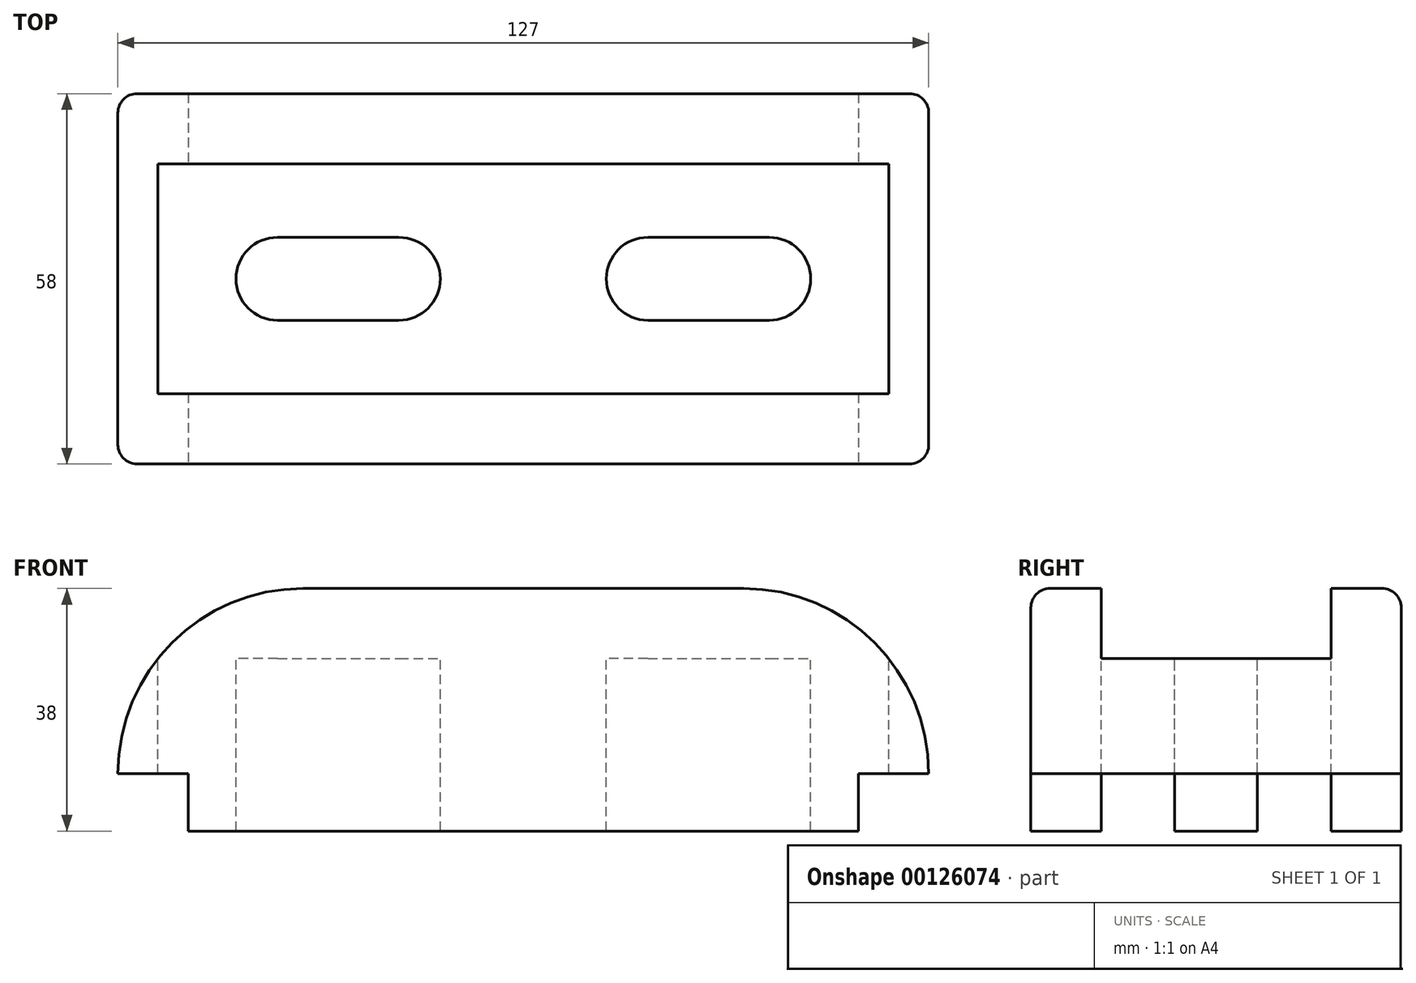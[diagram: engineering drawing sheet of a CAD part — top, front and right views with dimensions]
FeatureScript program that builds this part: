
annotation { "Feature Type Name" : "Feature", "Feature Type Description" : "" }
export const myFeature = defineFeature(function(context is Context, id is Id, definition is map)
    precondition{}
    {
        {
            var Q0;
            Q0=qCreatedBy(makeId("Front.planeOp"),FACE);
            var sketch = newSketch(context, id + "F0", { "sketchPlane" : qUnion([Q0])});
            skLineSegment(sketch, "E0", {"start": v(11, 0) * mm, "end": v(11, 9) * mm});
            skLineSegment(sketch, "E1", {"start": v(11, 9) * mm, "end": v(0, 9) * mm});
            skLineSegment(sketch, "E2", {"start": v(11, 0) * mm, "end": v(116, 0) * mm});
            skLineSegment(sketch, "E3", {"start": v(116, 0) * mm, "end": v(116, 9) * mm});
            skLineSegment(sketch, "E4", {"start": v(116, 9) * mm, "end": v(127, 9) * mm});
            skArc(sketch, "E5", {"start": v(29, 38) * mm, "mid": v(8.5, 29.5) * mm, "end": v(0, 9) * mm});
            skArc(sketch, "E6", {"start": v(127, 9) * mm, "mid": v(118.5, 29.5) * mm, "end": v(98, 38) * mm});
            skLineSegment(sketch, "E7", {"start": v(29, 38) * mm, "end": v(98, 38) * mm});
            skSolve(sketch);
        }
        {
            var Q0;
            Q0=makeQuery(id+"F0.imprint","IMPRINT",FACE,{"disambiguationData":[TD([[makeQuery(id+"F0.imprint","IMPRINT",EDGE,{"derivedFrom":sQuery(id+"F0.wireOp",EDGE,"E0")}),-1.0]])]});
            extrude(context, id + "F1", {"entities" : qUnion([Q0]), "oppositeDirection" : true, "depth" : 58 * mm});
        }
        {
            var Q0;
            Q0=qCreatedBy(makeId("Right.planeOp"),FACE);
            var sketch = newSketch(context, id + "F2", { "sketchPlane" : qUnion([Q0])});
            skLineSegment(sketch, "E8.bottom", {"start": v(11, 38) * mm, "end": v(47, 38) * mm});
            skLineSegment(sketch, "E8.top", {"start": v(11, 27) * mm, "end": v(47, 27) * mm});
            skLineSegment(sketch, "E8.left", {"start": v(11, 38) * mm, "end": v(11, 27) * mm});
            skLineSegment(sketch, "E8.right", {"start": v(47, 38) * mm, "end": v(47, 27) * mm});
            skSolve(sketch);
        }
        {
            var Q0;
            Q0 = qSketchRegion(id + "F2", true);
            extrude(context, id + "F3", {"entities" : qUnion([Q0]), "operationType" : NewBodyOperationType.REMOVE, "endBound" : BoundingType.THROUGH_ALL, "depth" : 25 * mm});
        }
        {
            var Q0;
            Q0=makeQuery(id+"F3.boolean.opBoolean","COPY",FACE,{"derivedFrom":makeQuery(id+"F3.opExtrude","SWEPT_FACE",FACE,{"disambiguationData":[OSD([sQuery(id+"F2.wireOp",EDGE,"E8.top")])]})});
            var sketch = newSketch(context, id + "F4", { "sketchPlane" : qUnion([Q0])});
            skLineSegment(sketch, "E9", {"start": v(25, 29) * mm, "end": v(44, 29) * mm, "construction": true});
            skLineSegment(sketch, "E10", {"start": v(83, 29) * mm, "end": v(102, 29) * mm, "construction": true});
            skArc(sketch, "E11.0.startCap", {"start": v(25, 22.5) * mm, "mid": v(18.5, 29) * mm, "end": v(25, 35.5) * mm});
            skArc(sketch, "E11.0.endCap", {"start": v(44, 35.5) * mm, "mid": v(50.5, 29) * mm, "end": v(44, 22.5) * mm});
            skLineSegment(sketch, "E11.0.left", {"start": v(25, 35.5) * mm, "end": v(44, 35.5) * mm});
            skLineSegment(sketch, "E11.0.right", {"start": v(25, 22.5) * mm, "end": v(44, 22.5) * mm});
            skArc(sketch, "E12.0.startCap", {"start": v(83, 22.5) * mm, "mid": v(76.5, 29) * mm, "end": v(83, 35.5) * mm});
            skArc(sketch, "E12.0.endCap", {"start": v(102, 35.5) * mm, "mid": v(108.5, 29) * mm, "end": v(102, 22.5) * mm});
            skLineSegment(sketch, "E12.0.left", {"start": v(83, 35.5) * mm, "end": v(102, 35.5) * mm});
            skLineSegment(sketch, "E12.0.right", {"start": v(83, 22.5) * mm, "end": v(102, 22.5) * mm});
            skSolve(sketch);
        }
        {
            var Q0;
            Q0=makeQuery(id+"F4.imprint","IMPRINT",FACE,{"disambiguationData":[TD([[makeQuery(id+"F4.imprint","IMPRINT",EDGE,{"derivedFrom":sQuery(id+"F4.wireOp",EDGE,"E12.0.startCap")}),-1.0]])]});
            var Q1;
            Q1=makeQuery(id+"F4.imprint","IMPRINT",FACE,{"disambiguationData":[TD([[makeQuery(id+"F4.imprint","IMPRINT",EDGE,{"derivedFrom":sQuery(id+"F4.wireOp",EDGE,"E11.0.startCap")}),-1.0]])]});
            extrude(context, id + "F5", {"entities" : qUnion([Q0, Q1]), "operationType" : NewBodyOperationType.REMOVE, "endBound" : BoundingType.THROUGH_ALL, "oppositeDirection" : true, "depth" : 25 * mm});
        }
        {
            var Q0;
            Q0=makeQuery(id+"F1.opExtrude","CAP_EDGE",EDGE,{"disambiguationData":[OSD([sQuery(id+"F0.wireOp",EDGE,"E6")])],"isStart":true});
            var Q1;
            Q1=makeQuery(id+"F1.opExtrude","CAP_EDGE",EDGE,{"disambiguationData":[OSD([sQuery(id+"F0.wireOp",EDGE,"E6")])],"isStart":false});
            fillet(context, id + "F6", {"entities" : qUnion([Q0, Q1]), "radius" : 3 * mm, "tangentPropagation" : true, "allowEdgeOverflow" : false});
        }
    });
